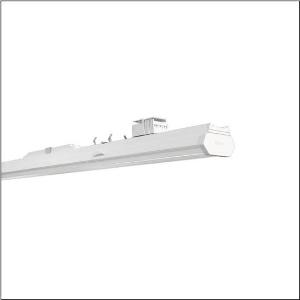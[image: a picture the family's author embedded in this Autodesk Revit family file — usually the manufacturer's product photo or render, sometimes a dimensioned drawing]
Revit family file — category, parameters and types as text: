
# Revit family: licross_r__21_protected_ho_52td13cn4c5s_0d58
name_source: partatom
category: Lighting Fixtures
units: mm (PartAtom-declared; Revit-internal decimal feet)

## family parameters
Cut with Voids When Loaded = No
Host = Face
Light Source = No
Part Type = Normal
Room Calculation Point = No
Round Connector Dimension = Use Diameter
Shared = No

## types (1)
- --- (1 x LED, 12680 lm, 68.9 W, 4000K)
    Apparent Load = 69 VA
    CIE Flux Codes = 89 96 99 100 99
    Color Rendering = 80
    Color Temperature = 4000K
    Default Elevation = 1800 mm
    Description = Licross® 21 Protected HO, luminaire insert, of sheet steel, galvanised, coil coated, white, length: 1.500mm, width: 66mm, height: 67mm, LED rated luminous flux: 12.690lm, light colour: 840, control gear: ON/OFF Multilumen, CLOi, control gear: ECG Multilumen, with plug, 3-pole, with phase selection, mains connection: 220..240V, AC, 50/60Hz, start of lifetime: 69W, end of service life: 83W, halogen-free wiring, primary light control with lens, of plastic, primary optical cover: cover, of PMMA, light emission: direct distribution, primary light characteristic: symmetric, protection rating (complete): IP54, insulation class (complete): insulation class I (protective earthing), certification: CE, ENEC, VDE, UKCA, protection symbol: D if used in an environment with non-conductive dust loads with corresponding accessories, impact resistance: IK06, permissible ambient temperature for indoor applications: -35..+35°C, corresponds to IFS (International Featured Standards) requirements for safety and quality in the food industry, reducing of maximum allowable ambient temperature of 5°C with ceiling mounting, LABS conformity tested according to VDMA 24364:2018-05, packaging unit: 1 piece
    Height = 92 mm
    Lamp = 1 x LED
    Lamp Light Flux = 12680 lm
    Lamp Power = 68.9 W
    Lamp count = 1
    Length = 1500 mm
    Luminous efficacy = 184 lm/W
    Manufacturer = Siteco
    ModVariant = No
    Model = 52TD13CN4C5S
    Mounting Place = Ceiling
    Mounting Type = Pendant
    Number of Poles = 1
    OnlyDefault = Yes
    Power Factor = 1
    Product Name = Licross® 21 Protected HO
    Product group = luminaire insert
    ProductGroupID = 901
    Protection Class = Protection class I
    Protection Degree = IP 54
    RLX_Detail_Level = 1
    RLX_Emergency_Light_Flux = 0 lm
    RLX_Emergency_Type = 0
    RLX_Emergency_Type_DB = No
    RlxData = <blob elided: 22033 chars, md5=1d28c04d>
    Socket = socket
    Standby Power = 0 W
    System Light Flux = 12680 lm
    System Power = 69 W
    Type Comments = factory setting: luminous flux: 100 % | (A | C | E) | 162 mA
    Type Image = l_1256148.jpg
    URL = http://relux.com
    VarID = @adj_059087
    Voltage = 0 V
    Weight = 0.00 kg
    Width = 88 mm

## geometry (parser evidence)
native form markers: Blend x4, Sweep x10
no freeform markers — native parametric forms only
